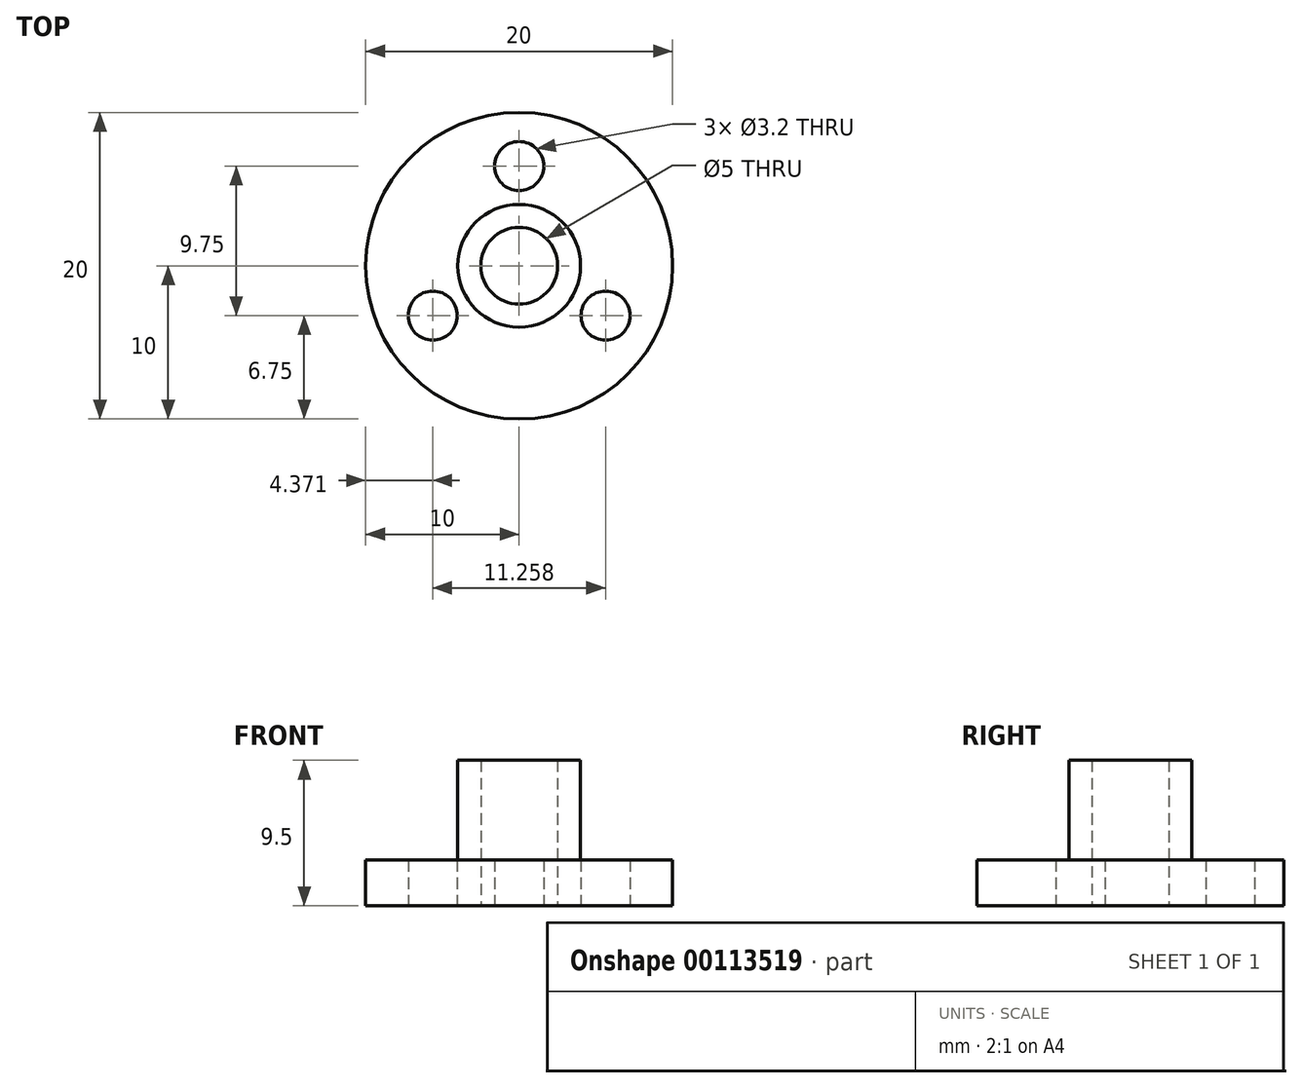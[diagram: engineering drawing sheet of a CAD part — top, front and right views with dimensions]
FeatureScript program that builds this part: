
annotation { "Feature Type Name" : "Feature", "Feature Type Description" : "" }
export const myFeature = defineFeature(function(context is Context, id is Id, definition is map)
    precondition{}
    {
        {
            assignVariable(context, id + "F0", {"name" : "FlangeHeight", "anyValue" : 3 * mm});
        }
        {
            assignVariable(context, id + "F1", {"name" : "NeckHeight", "anyValue" : 6.5 * mm});
        }
        {
            var Q0;
            Q0=qCreatedBy(makeId("Top.planeOp"),FACE);
            var sketch = newSketch(context, id + "F2", { "sketchPlane" : qUnion([Q0])});
            skCircle(sketch, "E0", {"center": v(0, 0) * mm, "radius": 2.5 * mm});
            skCircle(sketch, "E1", {"center": v(0, 0) * mm, "radius": 4 * mm});
            skCircle(sketch, "E2", {"center": v(0, 0) * mm, "radius": 10 * mm});
            skCircle(sketch, "E3", {"center": v(0, 6.5) * mm, "radius": 1.6 * mm});
            skCircle(sketch, "E4", {"center": v(-5.63, -3.25) * mm, "radius": 1.6 * mm});
            skLineSegment(sketch, "E5", {"start": v(0, 0) * mm, "end": v(0, 10) * mm, "construction": true});
            skLineSegment(sketch, "E6", {"start": v(0, 0) * mm, "end": v(-8.66, -5) * mm, "construction": true});
            skCircle(sketch, "E7", {"center": v(5.63, -3.25) * mm, "radius": 1.6 * mm});
            skSolve(sketch);
        }
        {
            var Q0;
            Q0=makeQuery(id+"F2.imprint","IMPRINT",FACE,{"disambiguationData":[TD([[makeQuery(id+"F2.imprint","IMPRINT",EDGE,{"derivedFrom":sQuery(id+"F2.wireOp",EDGE,"E1")}),-1.0]])]});
            var Q1;
            Q1=makeQuery(id+"F2.imprint","IMPRINT",FACE,{"disambiguationData":[TD([[makeQuery(id+"F2.imprint","IMPRINT",EDGE,{"derivedFrom":sQuery(id+"F2.wireOp",EDGE,"E0")}),-1.0]])]});
            extrude(context, id + "F3", {"entities" : qUnion([Q0, Q1]), "depth" : getVariable(context, 'FlangeHeight')});
        }
        {
            var Q0;
            Q0=makeQuery(id+"F2.imprint","IMPRINT",FACE,{"disambiguationData":[TD([[makeQuery(id+"F2.imprint","IMPRINT",EDGE,{"derivedFrom":sQuery(id+"F2.wireOp",EDGE,"E0")}),-1.0]])]});
            extrude(context, id + "F4", {"entities" : qUnion([Q0]), "operationType" : NewBodyOperationType.ADD, "depth" : getVariable(context, 'FlangeHeight') + getVariable(context, 'NeckHeight')});
        }
    });
